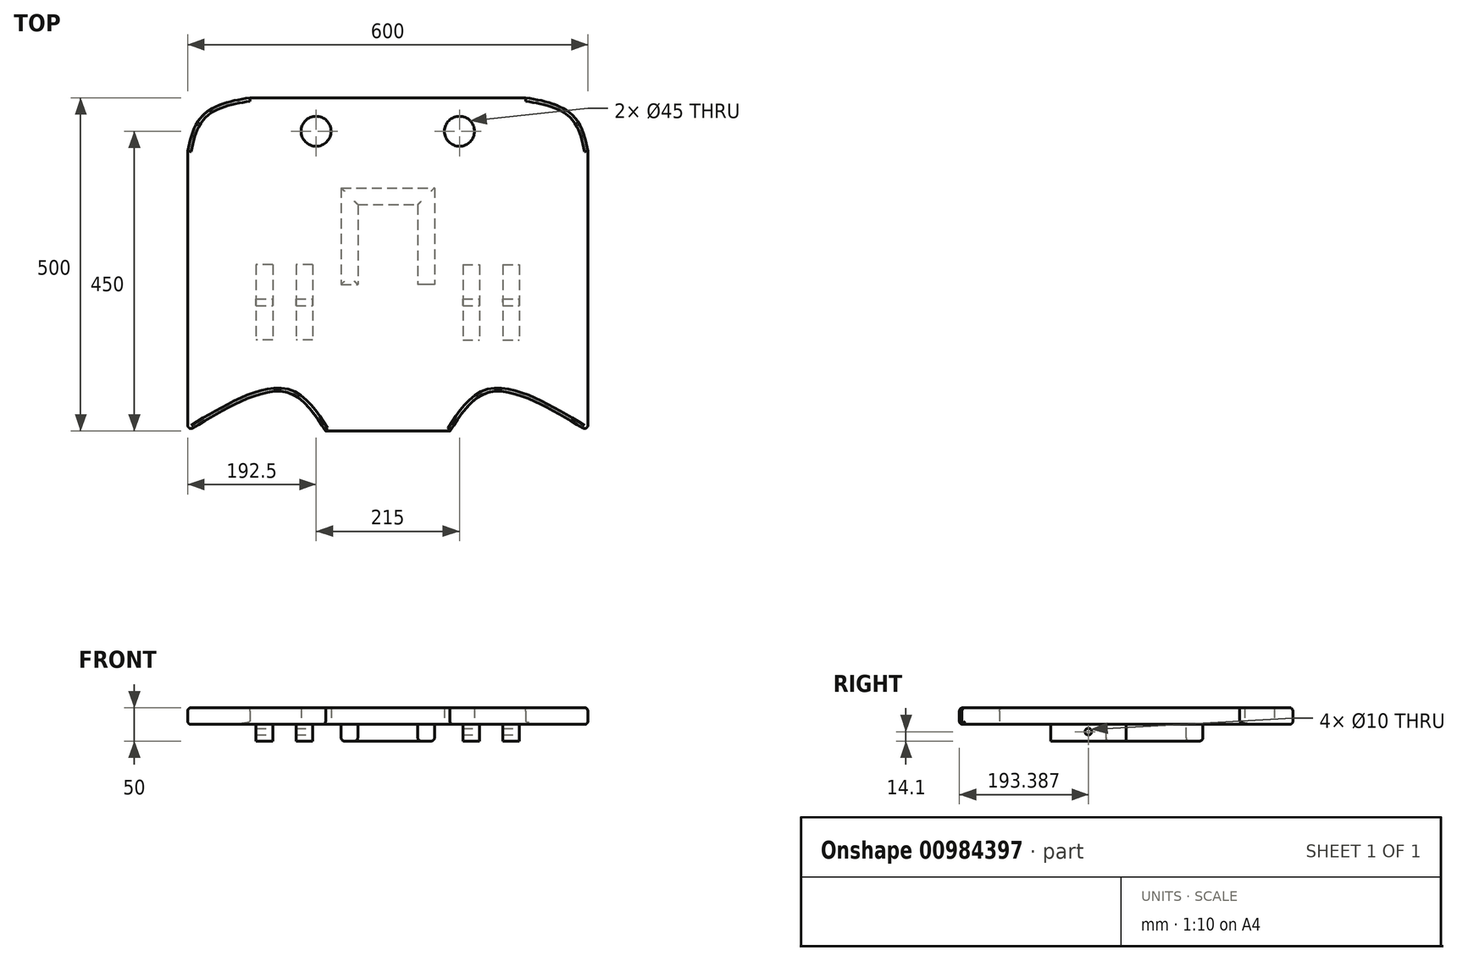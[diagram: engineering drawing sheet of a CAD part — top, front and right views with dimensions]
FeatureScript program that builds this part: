
annotation { "Feature Type Name" : "Feature", "Feature Type Description" : "" }
export const myFeature = defineFeature(function(context is Context, id is Id, definition is map)
    precondition{}
    {
        {
            var Q0;
            Q0=qCreatedBy(makeId("Top.planeOp"),FACE);
            var sketch = newSketch(context, id + "F0", { "sketchPlane" : qUnion([Q0])});
            skLineSegment(sketch, "E0.bottom", {"start": v(-300, 250) * mm, "end": v(300, 250) * mm});
            skLineSegment(sketch, "E0.top", {"start": v(-300, -250) * mm, "end": v(300, -250) * mm});
            skLineSegment(sketch, "E0.left", {"start": v(-300, 250) * mm, "end": v(-300, -250) * mm});
            skLineSegment(sketch, "E0.right", {"start": v(300, 250) * mm, "end": v(300, -250) * mm});
            skPoint(sketch, "E0.middle", {"position": v(0, 0) * mm});
            skLineSegment(sketch, "E1", {"start": v(-107.5, 250) * mm, "end": v(-107.5, 200) * mm});
            skLineSegment(sketch, "E2", {"start": v(-107.5, 200) * mm, "end": v(-300, 200) * mm});
            skLineSegment(sketch, "E3.MirrorCS", {"start": v(107.5, 250) * mm, "end": v(107.5, 200) * mm});
            skLineSegment(sketch, "E4.MirrorCS", {"start": v(107.5, 200) * mm, "end": v(300, 200) * mm});
            skCircle(sketch, "E5", {"center": v(-107.5, 200) * mm, "radius": 22.5 * mm});
            skCircle(sketch, "E6.MirrorC", {"center": v(107.5, 200) * mm, "radius": 22.5 * mm});
            skSolve(sketch);
        }
        {
            var Q0;
            Q0 = qSketchRegion(id + "F0", true);
            extrude(context, id + "F1", {"entities" : qUnion([Q0]), "depth" : 25 * mm, "offsetDistance" : 25 * mm});
        }
        {
            var Q0;
            Q0=makeQuery(id+"F1.opExtrude","CAP_FACE",FACE,{"disambiguationData":[OSD([sQuery(id+"F0.wireOp",EDGE,"E0.bottom"),sQuery(id+"F0.wireOp",EDGE,"E0.top"),sQuery(id+"F0.wireOp",EDGE,"E0.left"),sQuery(id+"F0.wireOp",EDGE,"E0.right"),sQuery(id+"F0.wireOp",EDGE,"E5"),sQuery(id+"F0.wireOp",EDGE,"E6.MirrorC")])],"isStart":true});
            var sketch = newSketch(context, id + "F2", { "sketchPlane" : qUnion([Q0])});
            skLineSegment(sketch, "E7", {"start": v(0, -250) * mm, "end": v(0, -115) * mm});
            skLineSegment(sketch, "E8.bottom", {"start": v(-70, -115) * mm, "end": v(70, -115) * mm});
            skLineSegment(sketch, "E8.top", {"start": v(-70, -90) * mm, "end": v(70, -90) * mm});
            skLineSegment(sketch, "E8.left", {"start": v(-70, -115) * mm, "end": v(-70, -90) * mm});
            skLineSegment(sketch, "E8.right", {"start": v(70, -115) * mm, "end": v(70, -90) * mm});
            skPoint(sketch, "E8.middle", {"position": v(0, -102.5) * mm});
            skLineSegment(sketch, "E9.bottom", {"start": v(70, -90) * mm, "end": v(45, -90) * mm});
            skLineSegment(sketch, "E9.top", {"start": v(70, 30) * mm, "end": v(45, 30) * mm});
            skLineSegment(sketch, "E9.left", {"start": v(70, -90) * mm, "end": v(70, 30) * mm});
            skLineSegment(sketch, "E9.right", {"start": v(45, -90) * mm, "end": v(45, 30) * mm});
            skLineSegment(sketch, "E10.MirrorCS", {"start": v(-45, -90) * mm, "end": v(-45, 30) * mm});
            skLineSegment(sketch, "E11.MirrorCS", {"start": v(-70, -90) * mm, "end": v(-70, 30) * mm});
            skLineSegment(sketch, "E12.MirrorCS", {"start": v(-70, 30) * mm, "end": v(-45, 30) * mm});
            skSolve(sketch);
        }
        {
            var Q0;
            Q0 = qSketchRegion(id + "F2", true);
            extrude(context, id + "F3", {"entities" : qUnion([Q0]), "operationType" : NewBodyOperationType.ADD, "depth" : 25 * mm, "offsetDistance" : 25 * mm});
        }
        {
            var Q0;
            Q0=makeQuery(id+"F1.opExtrude","CAP_FACE",FACE,{"disambiguationData":[OSD([sQuery(id+"F0.wireOp",EDGE,"E0.bottom"),sQuery(id+"F0.wireOp",EDGE,"E0.top"),sQuery(id+"F0.wireOp",EDGE,"E0.left"),sQuery(id+"F0.wireOp",EDGE,"E0.right"),sQuery(id+"F0.wireOp",EDGE,"E5"),sQuery(id+"F0.wireOp",EDGE,"E6.MirrorC")])],"isStart":true});
            var sketch = newSketch(context, id + "F4", { "sketchPlane" : qUnion([Q0])});
            skLineSegment(sketch, "E13", {"start": v(0, 250) * mm, "end": v(93.22, 250) * mm});
            skLineSegment(sketch, "E14.MirrorCS", {"start": v(0, 250) * mm, "end": v(-93.22, 250) * mm});
            skFitSpline(sketch, "E15", {"points": [v(93.22, 250) * mm, v(154.43, 191.03) * mm, v(300, 250) * mm], "startDerivative": vector(121.5, -190.3) * mm, "endDerivative": vector(283.83, 171.91) * mm});
            skFitSpline(sketch, "E16.MirrorCS", {"points": [v(-93.22, 250) * mm, v(-154.43, 191.03) * mm, v(-300, 250) * mm], "startDerivative": vector(-121.5, -190.3) * mm, "endDerivative": vector(-283.83, 171.91) * mm});
            skFitSpline(sketch, "E17", {"points": [v(0, -250) * mm, v(-267.42, -231.8) * mm, v(-300, -170.09) * mm], "startDerivative": vector(-505.65, -23.9) * mm, "endDerivative": vector(-44.5, 208.88) * mm});
            skFitSpline(sketch, "E18.MirrorCS", {"points": [v(0, -250) * mm, v(267.42, -231.8) * mm, v(300, -170.09) * mm], "startDerivative": vector(505.65, -23.9) * mm, "endDerivative": vector(44.5, 208.88) * mm});
            skSolve(sketch);
        }
        {
            var Q0;
            {var subQ0=sQuery(id+"F4.wireOp",EDGE,"E15");Q0=makeQuery(id+"F4.imprint","IMPRINT",FACE,{"disambiguationData":[TD([[makeQuery(id+"F4.imprint","IMPRINT",EDGE,{"derivedFrom":subQ0}),1.0]])]});}
            var Q1;
            {var subQ0=sQuery(id+"F4.wireOp",EDGE,"E16.MirrorCS");Q1=makeQuery(id+"F4.imprint","IMPRINT",FACE,{"disambiguationData":[TD([[makeQuery(id+"F4.imprint","IMPRINT",EDGE,{"derivedFrom":subQ0}),-1.0]])]});}
            var Q2;
            {var subQ0=sQuery(id+"F4.wireOp",EDGE,"E18.MirrorCS");var subQ1=makeQuery(id+"F1.opExtrude","CAP_EDGE",EDGE,{"disambiguationData":[OSD([sQuery(id+"F0.wireOp",EDGE,"E0.right")])],"isStart":true});var subQ2=makeQuery(id+"F4.imprint","INTERSECT",VERTEX,{"derivedFrom":[subQ1,subQ0]});Q2=makeQuery(id+"F4.imprint","IMPRINT",FACE,{"disambiguationData":[TD([[makeQuery(id+"F4.imprint","IMPRINT",EDGE,{"disambiguationData":[TD([[subQ2,1.0]])],"derivedFrom":subQ0}),-1.0]])]});}
            var Q3;
            {var subQ0=sQuery(id+"F4.wireOp",EDGE,"E17");var subQ1=makeQuery(id+"F1.opExtrude","CAP_EDGE",EDGE,{"disambiguationData":[OSD([sQuery(id+"F0.wireOp",EDGE,"E0.left")])],"isStart":true});var subQ2=makeQuery(id+"F4.imprint","INTERSECT",VERTEX,{"derivedFrom":[subQ1,subQ0]});Q3=makeQuery(id+"F4.imprint","IMPRINT",FACE,{"disambiguationData":[TD([[makeQuery(id+"F4.imprint","IMPRINT",EDGE,{"disambiguationData":[TD([[subQ2,1.0]])],"derivedFrom":subQ0}),1.0]])]});}
            extrude(context, id + "F5", {"entities" : qUnion([Q0, Q1, Q2, Q3]), "operationType" : NewBodyOperationType.REMOVE, "oppositeDirection" : true, "depth" : 30 * mm, "offsetDistance" : 25 * mm});
        }
        {
            var Q0;
            Q0=makeQuery(id+"F5.boolean.opBoolean","COPY",EDGE,{"derivedFrom":makeQuery(id+"F5.opExtrude","CAP_EDGE",EDGE,{"disambiguationData":[OSD([sQuery(id+"F4.wireOp",EDGE,"E18.MirrorCS")])],"isStart":true})});
            var Q1;
            Q1=makeQuery(id+"F1.opExtrude","CAP_EDGE",EDGE,{"disambiguationData":[OSD([sQuery(id+"F0.wireOp",EDGE,"E0.bottom")])],"isStart":true});
            var Q2;
            Q2=makeQuery(id+"F1.opExtrude","CAP_EDGE",EDGE,{"disambiguationData":[OSD([sQuery(id+"F0.wireOp",EDGE,"E0.right")])],"isStart":true});
            var Q3;
            Q3=makeQuery(id+"F5.boolean.opBoolean","COPY",EDGE,{"derivedFrom":makeQuery(id+"F5.opExtrude","CAP_EDGE",EDGE,{"disambiguationData":[OSD([sQuery(id+"F4.wireOp",EDGE,"E17")])],"isStart":true})});
            var Q4;
            Q4=makeQuery(id+"F1.opExtrude","CAP_EDGE",EDGE,{"disambiguationData":[OSD([sQuery(id+"F0.wireOp",EDGE,"E0.left")])],"isStart":true});
            var Q5;
            Q5=makeQuery(id+"F5.boolean.opBoolean","COPY",EDGE,{"derivedFrom":makeQuery(id+"F5.opExtrude","CAP_EDGE",EDGE,{"disambiguationData":[OSD([sQuery(id+"F4.wireOp",EDGE,"E16.MirrorCS")])],"isStart":true})});
            var Q6;
            Q6=makeQuery(id+"F1.opExtrude","CAP_EDGE",EDGE,{"disambiguationData":[OSD([sQuery(id+"F0.wireOp",EDGE,"E0.top")])],"isStart":true});
            var Q7;
            Q7=makeQuery(id+"F5.boolean.opBoolean","COPY",EDGE,{"derivedFrom":makeQuery(id+"F5.opExtrude","CAP_EDGE",EDGE,{"disambiguationData":[OSD([sQuery(id+"F4.wireOp",EDGE,"E15")])],"isStart":true})});
            var Q8;
            Q8=makeQuery(id+"F1.opExtrude","CAP_EDGE",EDGE,{"disambiguationData":[OSD([sQuery(id+"F0.wireOp",EDGE,"E0.right")])],"isStart":false});
            var Q9;
            Q9=makeQuery(id+"F5.boolean.opBoolean","INTERSECT",EDGE,{"derivedFrom":[makeQuery(id+"F1.opExtrude","CAP_FACE",FACE,{"disambiguationData":[OSD([sQuery(id+"F0.wireOp",EDGE,"E0.bottom"),sQuery(id+"F0.wireOp",EDGE,"E0.top"),sQuery(id+"F0.wireOp",EDGE,"E0.left"),sQuery(id+"F0.wireOp",EDGE,"E0.right"),sQuery(id+"F0.wireOp",EDGE,"E5"),sQuery(id+"F0.wireOp",EDGE,"E6.MirrorC")])],"isStart":false}),makeQuery(id+"F5.opExtrude","SWEPT_FACE",FACE,{"disambiguationData":[OSD([sQuery(id+"F4.wireOp",EDGE,"E15")])]})]});
            var Q10;
            Q10=makeQuery(id+"F1.opExtrude","CAP_EDGE",EDGE,{"disambiguationData":[OSD([sQuery(id+"F0.wireOp",EDGE,"E0.top")])],"isStart":false});
            var Q11;
            Q11=makeQuery(id+"F5.boolean.opBoolean","INTERSECT",EDGE,{"derivedFrom":[makeQuery(id+"F1.opExtrude","CAP_FACE",FACE,{"disambiguationData":[OSD([sQuery(id+"F0.wireOp",EDGE,"E0.bottom"),sQuery(id+"F0.wireOp",EDGE,"E0.top"),sQuery(id+"F0.wireOp",EDGE,"E0.left"),sQuery(id+"F0.wireOp",EDGE,"E0.right"),sQuery(id+"F0.wireOp",EDGE,"E5"),sQuery(id+"F0.wireOp",EDGE,"E6.MirrorC")])],"isStart":false}),makeQuery(id+"F5.opExtrude","SWEPT_FACE",FACE,{"disambiguationData":[OSD([sQuery(id+"F4.wireOp",EDGE,"E16.MirrorCS")])]})]});
            var Q12;
            Q12=makeQuery(id+"F1.opExtrude","CAP_EDGE",EDGE,{"disambiguationData":[OSD([sQuery(id+"F0.wireOp",EDGE,"E0.left")])],"isStart":false});
            var Q13;
            Q13=makeQuery(id+"F5.boolean.opBoolean","INTERSECT",EDGE,{"derivedFrom":[makeQuery(id+"F1.opExtrude","CAP_FACE",FACE,{"disambiguationData":[OSD([sQuery(id+"F0.wireOp",EDGE,"E0.bottom"),sQuery(id+"F0.wireOp",EDGE,"E0.top"),sQuery(id+"F0.wireOp",EDGE,"E0.left"),sQuery(id+"F0.wireOp",EDGE,"E0.right"),sQuery(id+"F0.wireOp",EDGE,"E5"),sQuery(id+"F0.wireOp",EDGE,"E6.MirrorC")])],"isStart":false}),makeQuery(id+"F5.opExtrude","SWEPT_FACE",FACE,{"disambiguationData":[OSD([sQuery(id+"F4.wireOp",EDGE,"E18.MirrorCS")])]})]});
            var Q14;
            Q14=makeQuery(id+"F1.opExtrude","CAP_EDGE",EDGE,{"disambiguationData":[OSD([sQuery(id+"F0.wireOp",EDGE,"E0.bottom")])],"isStart":false});
            var Q15;
            Q15=makeQuery(id+"F5.boolean.opBoolean","INTERSECT",EDGE,{"derivedFrom":[makeQuery(id+"F1.opExtrude","CAP_FACE",FACE,{"disambiguationData":[OSD([sQuery(id+"F0.wireOp",EDGE,"E0.bottom"),sQuery(id+"F0.wireOp",EDGE,"E0.top"),sQuery(id+"F0.wireOp",EDGE,"E0.left"),sQuery(id+"F0.wireOp",EDGE,"E0.right"),sQuery(id+"F0.wireOp",EDGE,"E5"),sQuery(id+"F0.wireOp",EDGE,"E6.MirrorC")])],"isStart":false}),makeQuery(id+"F5.opExtrude","SWEPT_FACE",FACE,{"disambiguationData":[OSD([sQuery(id+"F4.wireOp",EDGE,"E17")])]})]});
            var Q16;
            Q16=makeQuery(id+"F5.boolean.opBoolean","COPY",EDGE,{"derivedFrom":makeQuery(id+"F5.opExtrude","SWEPT_EDGE",EDGE,{"disambiguationData":[OSD([sQuery(id+"F0.wireOp",EDGE,"E0.left"),sQuery(id+"F4.wireOp",EDGE,"E17")])]})});
            var Q17;
            Q17=makeQuery(id+"F5.boolean.opBoolean","COPY",EDGE,{"derivedFrom":makeQuery(id+"F5.opExtrude","SWEPT_EDGE",EDGE,{"disambiguationData":[OSD([sQuery(id+"F0.wireOp",EDGE,"E0.bottom"),sQuery(id+"F4.wireOp",EDGE,"E17")])]})});
            var Q18;
            Q18=makeQuery(id+"F5.boolean.opBoolean","COPY",EDGE,{"derivedFrom":makeQuery(id+"F5.opExtrude","SWEPT_EDGE",EDGE,{"disambiguationData":[OSD([sQuery(id+"F0.wireOp",EDGE,"E0.bottom"),sQuery(id+"F4.wireOp",EDGE,"E18.MirrorCS")])]})});
            var Q19;
            Q19=makeQuery(id+"F5.boolean.opBoolean","COPY",EDGE,{"derivedFrom":makeQuery(id+"F5.opExtrude","SWEPT_EDGE",EDGE,{"disambiguationData":[OSD([sQuery(id+"F0.wireOp",EDGE,"E0.right"),sQuery(id+"F4.wireOp",EDGE,"E18.MirrorCS")])]})});
            var Q20;
            Q20=makeQuery(id+"F5.boolean.opBoolean","COPY",EDGE,{"derivedFrom":makeQuery(id+"F5.opExtrude","SWEPT_EDGE",EDGE,{"disambiguationData":[OSD([sQuery(id+"F0.wireOp",EDGE,"E0.top"),sQuery(id+"F4.wireOp",EDGE,"E13"),sQuery(id+"F4.wireOp",EDGE,"E15")])]})});
            var Q21;
            {var subQ0=sQuery(id+"F0.wireOp",EDGE,"E0.right");var subQ1=sQuery(id+"F0.wireOp",EDGE,"E0.top");Q21=makeQuery(id+"F5.boolean.opBoolean","MERGE",EDGE,{"derivedFrom":[makeQuery(id+"F1.opExtrude","SWEPT_EDGE",EDGE,{"disambiguationData":[OSD([subQ1,subQ0])]})],"fromTools":[makeQuery(id+"F5.opExtrude","SWEPT_EDGE",EDGE,{"disambiguationData":[OSD([subQ1,subQ0,sQuery(id+"F4.wireOp",EDGE,"E15")])]})]});}
            var Q22;
            Q22=makeQuery(id+"F5.boolean.opBoolean","COPY",EDGE,{"derivedFrom":makeQuery(id+"F5.opExtrude","SWEPT_EDGE",EDGE,{"disambiguationData":[OSD([sQuery(id+"F0.wireOp",EDGE,"E0.top"),sQuery(id+"F4.wireOp",EDGE,"E14.MirrorCS"),sQuery(id+"F4.wireOp",EDGE,"E16.MirrorCS")])]})});
            var Q23;
            {var subQ0=sQuery(id+"F0.wireOp",EDGE,"E0.left");var subQ1=sQuery(id+"F0.wireOp",EDGE,"E0.top");Q23=makeQuery(id+"F5.boolean.opBoolean","MERGE",EDGE,{"derivedFrom":[makeQuery(id+"F1.opExtrude","SWEPT_EDGE",EDGE,{"disambiguationData":[OSD([subQ1,subQ0])]})],"fromTools":[makeQuery(id+"F5.opExtrude","SWEPT_EDGE",EDGE,{"disambiguationData":[OSD([subQ1,subQ0,sQuery(id+"F4.wireOp",EDGE,"E16.MirrorCS")])]})]});}
            fillet(context, id + "F6", {"entities" : qUnion([Q0, Q1, Q2, Q3, Q4, Q5, Q6, Q7, Q8, Q9, Q10, Q11, Q12, Q13, Q14, Q15, Q16, Q17, Q18, Q19, Q20, Q21, Q22, Q23]), "radius" : 5 * mm, "tangentPropagation" : true, "allowEdgeOverflow" : false});
        }
        {
            var Q0;
            Q0=makeQuery(id+"F3.opExtrude","CAP_EDGE",EDGE,{"disambiguationData":[OSD([sQuery(id+"F2.wireOp",EDGE,"E8.right"),sQuery(id+"F2.wireOp",EDGE,"E9.left")])],"isStart":false});
            var Q1;
            Q1=makeQuery(id+"F3.opExtrude","CAP_EDGE",EDGE,{"disambiguationData":[OSD([sQuery(id+"F2.wireOp",EDGE,"E9.right")])],"isStart":false});
            var Q2;
            Q2=makeQuery(id+"F3.opExtrude","CAP_EDGE",EDGE,{"disambiguationData":[OSD([sQuery(id+"F2.wireOp",EDGE,"E8.top")])],"isStart":false});
            var Q3;
            Q3=makeQuery(id+"F3.opExtrude","CAP_EDGE",EDGE,{"disambiguationData":[OSD([sQuery(id+"F2.wireOp",EDGE,"E10.MirrorCS")])],"isStart":false});
            var Q4;
            Q4=makeQuery(id+"F3.opExtrude","CAP_EDGE",EDGE,{"disambiguationData":[OSD([sQuery(id+"F2.wireOp",EDGE,"E12.MirrorCS")])],"isStart":false});
            var Q5;
            Q5=makeQuery(id+"F3.opExtrude","CAP_EDGE",EDGE,{"disambiguationData":[OSD([sQuery(id+"F2.wireOp",EDGE,"E8.left"),sQuery(id+"F2.wireOp",EDGE,"E11.MirrorCS")])],"isStart":false});
            var Q6;
            Q6=makeQuery(id+"F3.opExtrude","CAP_EDGE",EDGE,{"disambiguationData":[OSD([sQuery(id+"F2.wireOp",EDGE,"E8.bottom")])],"isStart":false});
            fillet(context, id + "F7", {"entities" : qUnion([Q0, Q1, Q2, Q3, Q4, Q5, Q6]), "radius" : 5 * mm, "tangentPropagation" : true, "allowEdgeOverflow" : false});
        }
        {
            var Q0;
            Q0=makeQuery(id+"F1.opExtrude","CAP_FACE",FACE,{"disambiguationData":[OSD([sQuery(id+"F0.wireOp",EDGE,"E0.bottom"),sQuery(id+"F0.wireOp",EDGE,"E0.top"),sQuery(id+"F0.wireOp",EDGE,"E0.left"),sQuery(id+"F0.wireOp",EDGE,"E0.right"),sQuery(id+"F0.wireOp",EDGE,"E5"),sQuery(id+"F0.wireOp",EDGE,"E6.MirrorC")])],"isStart":true});
            var sketch = newSketch(context, id + "F8", { "sketchPlane" : qUnion([Q0])});
            skLineSegment(sketch, "E19", {"start": v(295, 56.61) * mm, "end": v(185, 56.61) * mm});
            skLineSegment(sketch, "E20.bottom", {"start": v(172.5, 0.28) * mm, "end": v(197.5, 0.28) * mm});
            skLineSegment(sketch, "E20.top", {"start": v(172.5, 112.95) * mm, "end": v(197.5, 112.95) * mm});
            skLineSegment(sketch, "E20.left", {"start": v(172.5, 0.28) * mm, "end": v(172.5, 112.95) * mm});
            skLineSegment(sketch, "E20.right", {"start": v(197.5, 0.28) * mm, "end": v(197.5, 112.95) * mm});
            skPoint(sketch, "E20.middle", {"position": v(185, 56.61) * mm});
            skLineSegment(sketch, "E21", {"start": v(185, 56.61) * mm, "end": v(125, 56.61) * mm});
            skPoint(sketch, "E21.endSnap0", {"position": v(172.5, 56.61) * mm});
            skLineSegment(sketch, "E22.bottom", {"start": v(112.5, 0.28) * mm, "end": v(137.5, 0.28) * mm});
            skLineSegment(sketch, "E22.top", {"start": v(112.5, 112.95) * mm, "end": v(137.5, 112.95) * mm});
            skLineSegment(sketch, "E22.left", {"start": v(112.5, 0.28) * mm, "end": v(112.5, 112.95) * mm});
            skLineSegment(sketch, "E22.right", {"start": v(137.5, 0.28) * mm, "end": v(137.5, 112.95) * mm});
            skPoint(sketch, "E22.middle", {"position": v(125, 56.61) * mm});
            skLineSegment(sketch, "E23.MirrorCS", {"start": v(-112.5, 0.28) * mm, "end": v(-112.5, 112.95) * mm});
            skLineSegment(sketch, "E24.MirrorCS", {"start": v(-112.5, 0.28) * mm, "end": v(-137.5, 0.28) * mm});
            skLineSegment(sketch, "E25.MirrorCS", {"start": v(-137.5, 0.28) * mm, "end": v(-137.5, 112.95) * mm});
            skLineSegment(sketch, "E26.MirrorCS", {"start": v(-112.5, 112.95) * mm, "end": v(-137.5, 112.95) * mm});
            skLineSegment(sketch, "E27.MirrorCS", {"start": v(-172.5, 0.28) * mm, "end": v(-172.5, 112.95) * mm});
            skLineSegment(sketch, "E28.MirrorCS", {"start": v(-172.5, 112.95) * mm, "end": v(-197.5, 112.95) * mm});
            skLineSegment(sketch, "E29.MirrorCS", {"start": v(-197.5, 0.28) * mm, "end": v(-197.5, 112.95) * mm});
            skLineSegment(sketch, "E30.MirrorCS", {"start": v(-172.5, 0.28) * mm, "end": v(-197.5, 0.28) * mm});
            skSolve(sketch);
        }
        {
            var Q0;
            Q0 = qSketchRegion(id + "F8", true);
            extrude(context, id + "F9", {"entities" : qUnion([Q0]), "operationType" : NewBodyOperationType.ADD, "depth" : 25 * mm, "offsetDistance" : 25 * mm});
        }
        {
            var Q0;
            Q0=makeQuery(id+"F9.opExtrude","SWEPT_FACE",FACE,{"disambiguationData":[OSD([sQuery(id+"F8.wireOp",EDGE,"E20.right")])]});
            var sketch = newSketch(context, id + "F10", { "sketchPlane" : qUnion([Q0])});
            skCircle(sketch, "E31", {"center": v(-56.61, -10.9) * mm, "radius": 5 * mm});
            skPoint(sketch, "E31.centerSnap0", {"position": v(-56.61, 0) * mm});
            skSolve(sketch);
        }
        {
            var Q0;
            Q0 = qSketchRegion(id + "F10", true);
            extrude(context, id + "F11", {"entities" : qUnion([Q0]), "operationType" : NewBodyOperationType.REMOVE, "oppositeDirection" : true, "depth" : 800 * mm, "offsetDistance" : 25 * mm});
        }
    });
